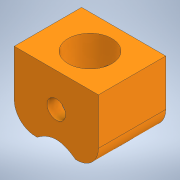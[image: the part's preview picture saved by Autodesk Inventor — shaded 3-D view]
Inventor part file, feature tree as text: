
AUTODESK INVENTOR PART (.ipt)
format: ipt  version: 2022 (Build 260153000, 153)  size: 176,128 bytes
history: native  units: mm
features: extrude x4, sketch x4, chamfer x1, fillet x1
ambient origin geometry x8: Origin, YZ Plane, XZ Plane, XY Plane, X Axis, Y Axis, Z Axis, Center Point
bodies: Solid1 (feature_tree)
feature tree (10):
  extrude  "Extrusion1"  Depth=10.0mm
  extrude  "Extrusion2"  Depth=8.0mm
  chamfer  "Chamfer1"  [1 undecoded]
  extrude  "Extrusion3"  Depth=2.2mm
  fillet  "Fillet1"  [1 undecoded]
  extrude  "Extrusion4"  Depth=8.0mm
  sketch  "Sketch1"  dims[d0=10.0mm d1=10.0mm]
  sketch  "Sketch2"  dims[d2=8.0mm d3=0.0mm d4=5.2mm d5=0.0mm d6=0.0mm]
  sketch  "Sketch3"  dims[d7=2.0mm d8=3.0mm d9=45.0deg d10=2.2mm d11=0.0mm d12=0.0mm]
  sketch  "Sketch4"  dims[d13=2.5mm d14=3.0mm d15=8.0mm d16=0.0mm d17=0.0mm d18=8.0mm]
note: 2 required parameter values undecoded (feature->parameter linkage not recoverable at this tier; creation-order binding heuristic only, values carry confidence <= 0.55)
